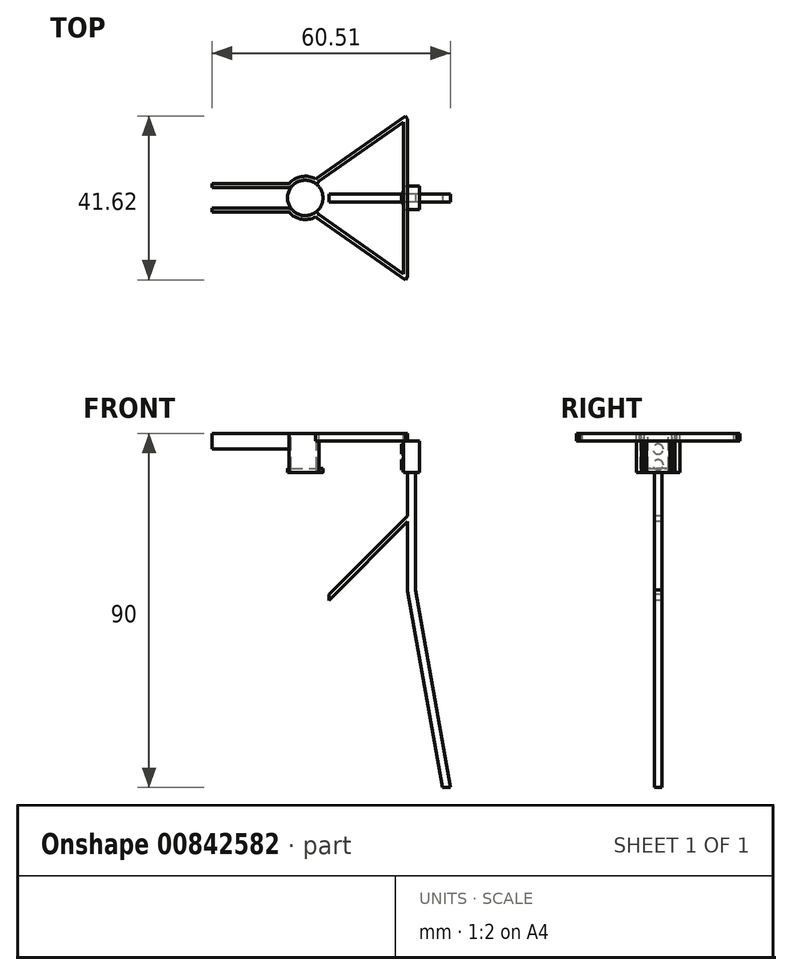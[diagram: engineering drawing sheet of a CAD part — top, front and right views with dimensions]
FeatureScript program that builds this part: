
annotation { "Feature Type Name" : "Feature", "Feature Type Description" : "" }
export const myFeature = defineFeature(function(context is Context, id is Id, definition is map)
    precondition{}
    {
        {
            var Q0;
            Q0=qCreatedBy(makeId("Top.planeOp"),FACE);
            var sketch = newSketch(context, id + "F0", { "sketchPlane" : qUnion([Q0])});
            skLineSegment(sketch, "E0", {"start": v(-23.66, -3.63) * mm, "end": v(-23.66, -2.63) * mm});
            skLineSegment(sketch, "E1", {"start": v(-23.66, -2.63) * mm, "end": v(-3.66, -2.63) * mm});
            skLineSegment(sketch, "E2", {"start": v(-4.14, -3.63) * mm, "end": v(-23.66, -3.63) * mm});
            skArc(sketch, "E3", {"start": v(-3.66, -2.63) * mm, "mid": v(-0.56, -4.46) * mm, "end": v(2.9, -3.45) * mm});
            skArc(sketch, "E4", {"start": v(-4.14, -3.62) * mm, "mid": v(-0.42, -5.48) * mm, "end": v(3.54, -4.21) * mm});
            skLineSegment(sketch, "E5", {"start": v(3.54, -4.21) * mm, "end": v(2.9, -3.45) * mm});
            skLineSegment(sketch, "E6", {"start": v(2.65, -4.82) * mm, "end": v(25.43, -20.81) * mm});
            skLineSegment(sketch, "E7", {"start": v(26, -20) * mm, "end": v(25.43, -20.81) * mm});
            skLineSegment(sketch, "E8", {"start": v(26, -20) * mm, "end": v(3.54, -4.21) * mm});
            skLineSegment(sketch, "E9", {"start": v(3, -3) * mm, "end": v(9.13, -8.14) * mm, "construction": true});
            skLineSegment(sketch, "E10", {"start": v(-4.14, -3.63) * mm, "end": v(-3.66, -2.63) * mm});
            skLineSegment(sketch, "E11.bottom", {"start": v(26, -20) * mm, "end": v(25, -20) * mm});
            skLineSegment(sketch, "E11.top", {"start": v(26, 0) * mm, "end": v(25, 0) * mm});
            skLineSegment(sketch, "E11.left", {"start": v(26, -20) * mm, "end": v(26, 0) * mm});
            skLineSegment(sketch, "E11.right", {"start": v(25, -20) * mm, "end": v(25, 0) * mm});
            skSolve(sketch);
        }
        {
            var Q0;
            Q0 = qSketchRegion(id + "F0", true);
            extrude(context, id + "F1", {"entities" : qUnion([Q0]), "oppositeDirection" : true, "depth" : 2 * mm, "offsetDistance" : 25 * mm});
        }
        {
            var Q0;
            Q0=makeQuery(id+"F0.imprint","IMPRINT",FACE,{"disambiguationData":[TD([[makeQuery(id+"F0.imprint","IMPRINT",EDGE,{"derivedFrom":sQuery(id+"F0.wireOp",EDGE,"E0")}),-1.0]])]});
            var Q1;
            Q1=makeQuery(id+"F0.imprint","IMPRINT",FACE,{"disambiguationData":[TD([[makeQuery(id+"F0.imprint","IMPRINT",EDGE,{"derivedFrom":sQuery(id+"F0.wireOp",EDGE,"E3")}),-1.0]])]});
            extrude(context, id + "F2", {"entities" : qUnion([Q0, Q1]), "operationType" : NewBodyOperationType.ADD, "oppositeDirection" : true, "depth" : 4 * mm, "offsetDistance" : 25 * mm});
        }
        {
            var Q0;
            Q0=makeQuery(id+"F0.imprint","IMPRINT",FACE,{"disambiguationData":[TD([[makeQuery(id+"F0.imprint","IMPRINT",EDGE,{"derivedFrom":sQuery(id+"F0.wireOp",EDGE,"E3")}),-1.0]])]});
            extrude(context, id + "F3", {"entities" : qUnion([Q0]), "operationType" : NewBodyOperationType.ADD, "oppositeDirection" : true, "depth" : 10 * mm, "offsetDistance" : 25 * mm});
        }
        {
            var Q0;
            Q0=makeQuery(id+"F1.opExtrude","SWEPT_BODY",BODY,{"disambiguationData":[OSD([sQuery(id+"F0.wireOp",EDGE,"E0"),sQuery(id+"F0.wireOp",EDGE,"E1"),sQuery(id+"F0.wireOp",EDGE,"E2"),sQuery(id+"F0.wireOp",EDGE,"E3"),sQuery(id+"F0.wireOp",EDGE,"E4"),sQuery(id+"F0.wireOp",EDGE,"E5"),sQuery(id+"F0.wireOp",EDGE,"E6"),sQuery(id+"F0.wireOp",EDGE,"E7"),sQuery(id+"F0.wireOp",EDGE,"E8"),sQuery(id+"F0.wireOp",EDGE,"E11.top"),sQuery(id+"F0.wireOp",EDGE,"E11.left"),sQuery(id+"F0.wireOp",EDGE,"E11.right")])]});
            var Q1;
            Q1=qCreatedBy(makeId("Front.planeOp"),FACE);
            mirror(context, id + "F4", {"operationType" : NewBodyOperationType.ADD, "entities" : qUnion([Q0]), "mirrorPlane" : qUnion([Q1])});
        }
        {
            var Q0;
            Q0=makeQuery(id+"F3.opExtrude","CAP_FACE",FACE,{"disambiguationData":[OSD([sQuery(id+"F0.wireOp",EDGE,"E3"),sQuery(id+"F0.wireOp",EDGE,"E4"),sQuery(id+"F0.wireOp",EDGE,"E5"),sQuery(id+"F0.wireOp",EDGE,"E10")])],"isStart":false});
            var sketch = newSketch(context, id + "F5", { "sketchPlane" : qUnion([Q0])});
            skCircle(sketch, "E12", {"center": v(0, 0) * mm, "radius": 4.5 * mm});
            skSolve(sketch);
        }
        {
            var Q0;
            Q0 = qSketchRegion(id + "F5", true);
            extrude(context, id + "F6", {"entities" : qUnion([Q0]), "operationType" : NewBodyOperationType.ADD, "oppositeDirection" : true, "depth" : 1 * mm, "offsetDistance" : 25 * mm});
        }
        {
            var Q0;
            {var subQ0=makeQuery(id+"F1.opExtrude","SWEPT_FACE",FACE,{"disambiguationData":[OSD([sQuery(id+"F0.wireOp",EDGE,"E11.left")])]});Q0=makeQuery(id+"F4.boolean.opBoolean","MERGE",FACE,{"derivedFrom":[subQ0,makeQuery(id+"F4.opPattern","COPY",FACE,{"derivedFrom":subQ0,"instanceName":"1"})]});}
            var sketch = newSketch(context, id + "F7", { "sketchPlane" : qUnion([Q0])});
            skLineSegment(sketch, "E13.bottom", {"start": v(-3, -2) * mm, "end": v(3, -2) * mm});
            skLineSegment(sketch, "E13.top", {"start": v(-3, -10) * mm, "end": v(3, -10) * mm});
            skLineSegment(sketch, "E13.left", {"start": v(-3, -2) * mm, "end": v(-3, -10) * mm});
            skLineSegment(sketch, "E13.right", {"start": v(3, -2) * mm, "end": v(3, -10) * mm});
            skCircle(sketch, "E14", {"center": v(0, -4) * mm, "radius": 1.3 * mm});
            skCircle(sketch, "E15", {"center": v(0, -8) * mm, "radius": 1.3 * mm});
            skLineSegment(sketch, "E16", {"start": v(-3, -6) * mm, "end": v(3, -6) * mm, "construction": true});
            skSolve(sketch);
        }
        {
            var Q0;
            Q0 = qSketchRegion(id + "F7", true);
            var Q1;
            {var subQ0=makeQuery(id+"F1.opExtrude","SWEPT_FACE",FACE,{"disambiguationData":[OSD([sQuery(id+"F0.wireOp",EDGE,"E11.right")])]});Q1=makeQuery(id+"F4.boolean.opBoolean","MERGE",FACE,{"derivedFrom":[subQ0,makeQuery(id+"F4.opPattern","COPY",FACE,{"derivedFrom":subQ0,"instanceName":"1"})]});}
            extrude(context, id + "F8", {"entities" : qUnion([Q0]), "operationType" : NewBodyOperationType.ADD, "endBound" : BoundingType.UP_TO_SURFACE, "oppositeDirection" : true, "depth" : 25 * mm, "endBoundEntityFace" : qUnion([Q1]), "offsetDistance" : 25 * mm});
        }
        {
            var Q0;
            Q0=makeQuery(id+"F7.imprint","IMPRINT",FACE,{"disambiguationData":[TD([[makeQuery(id+"F7.imprint","IMPRINT",EDGE,{"derivedFrom":sQuery(id+"F7.wireOp",EDGE,"E13.bottom")}),-1.0]])]});
            var Q1;
            Q1=makeQuery(id+"F7.imprint","IMPRINT",FACE,{"disambiguationData":[TD([[makeQuery(id+"F7.imprint","IMPRINT",EDGE,{"derivedFrom":sQuery(id+"F7.wireOp",EDGE,"E14")}),1.0]])]});
            var Q2;
            Q2=makeQuery(id+"F7.imprint","IMPRINT",FACE,{"disambiguationData":[TD([[makeQuery(id+"F7.imprint","IMPRINT",EDGE,{"derivedFrom":sQuery(id+"F7.wireOp",EDGE,"E15")}),1.0]])]});
            extrude(context, id + "F9", {"entities" : qUnion([Q0, Q1, Q2]), "depth" : 3 * mm, "offsetDistance" : 25 * mm});
        }
        {
            var Q0;
            Q0=makeQuery(id+"F7.imprint","IMPRINT",FACE,{"disambiguationData":[TD([[makeQuery(id+"F7.imprint","IMPRINT",EDGE,{"derivedFrom":sQuery(id+"F7.wireOp",EDGE,"E14")}),1.0]])]});
            var Q1;
            Q1=makeQuery(id+"F7.imprint","IMPRINT",FACE,{"disambiguationData":[TD([[makeQuery(id+"F7.imprint","IMPRINT",EDGE,{"derivedFrom":sQuery(id+"F7.wireOp",EDGE,"E15")}),1.0]])]});
            extrude(context, id + "F10", {"entities" : qUnion([Q0, Q1]), "operationType" : NewBodyOperationType.ADD, "oppositeDirection" : true, "depth" : 1.5 * mm, "offsetDistance" : 25 * mm});
        }
        {
            var Q0;
            Q0=qCreatedBy(makeId("Front.planeOp"),FACE);
            var sketch = newSketch(context, id + "F11", { "sketchPlane" : qUnion([Q0])});
            skLineSegment(sketch, "E17", {"start": v(26, -10) * mm, "end": v(26, -21) * mm});
            skLineSegment(sketch, "E18", {"start": v(26, -21) * mm, "end": v(6, -41) * mm});
            skLineSegment(sketch, "E19", {"start": v(6, -41) * mm, "end": v(6, -42.41) * mm});
            skLineSegment(sketch, "E20", {"start": v(6, -42.41) * mm, "end": v(26, -22.41) * mm});
            skLineSegment(sketch, "E21", {"start": v(26, -22.41) * mm, "end": v(26, -40) * mm});
            skLineSegment(sketch, "E22", {"start": v(26, -40) * mm, "end": v(34.82, -90) * mm});
            skLineSegment(sketch, "E23", {"start": v(34.82, -90) * mm, "end": v(36.85, -90) * mm});
            skLineSegment(sketch, "E24", {"start": v(36.85, -90) * mm, "end": v(28, -39.83) * mm});
            skLineSegment(sketch, "E25", {"start": v(28, -39.83) * mm, "end": v(28, -10) * mm});
            skLineSegment(sketch, "E26", {"start": v(28, -10) * mm, "end": v(26, -10) * mm});
            skLineSegment(sketch, "E27", {"start": v(34.82, -90) * mm, "end": v(36.79, -89.65) * mm, "construction": true});
            skLineSegment(sketch, "E28", {"start": v(6, -41) * mm, "end": v(6.7, -41.7) * mm, "construction": true});
            skSolve(sketch);
        }
        {
            var Q0;
            Q0 = qSketchRegion(id + "F11", true);
            extrude(context, id + "F12", {"entities" : qUnion([Q0]), "operationType" : NewBodyOperationType.ADD, "endBound" : BoundingType.SYMMETRIC, "oppositeDirection" : true, "depth" : 2 * mm, "offsetDistance" : 25 * mm});
        }
    });
